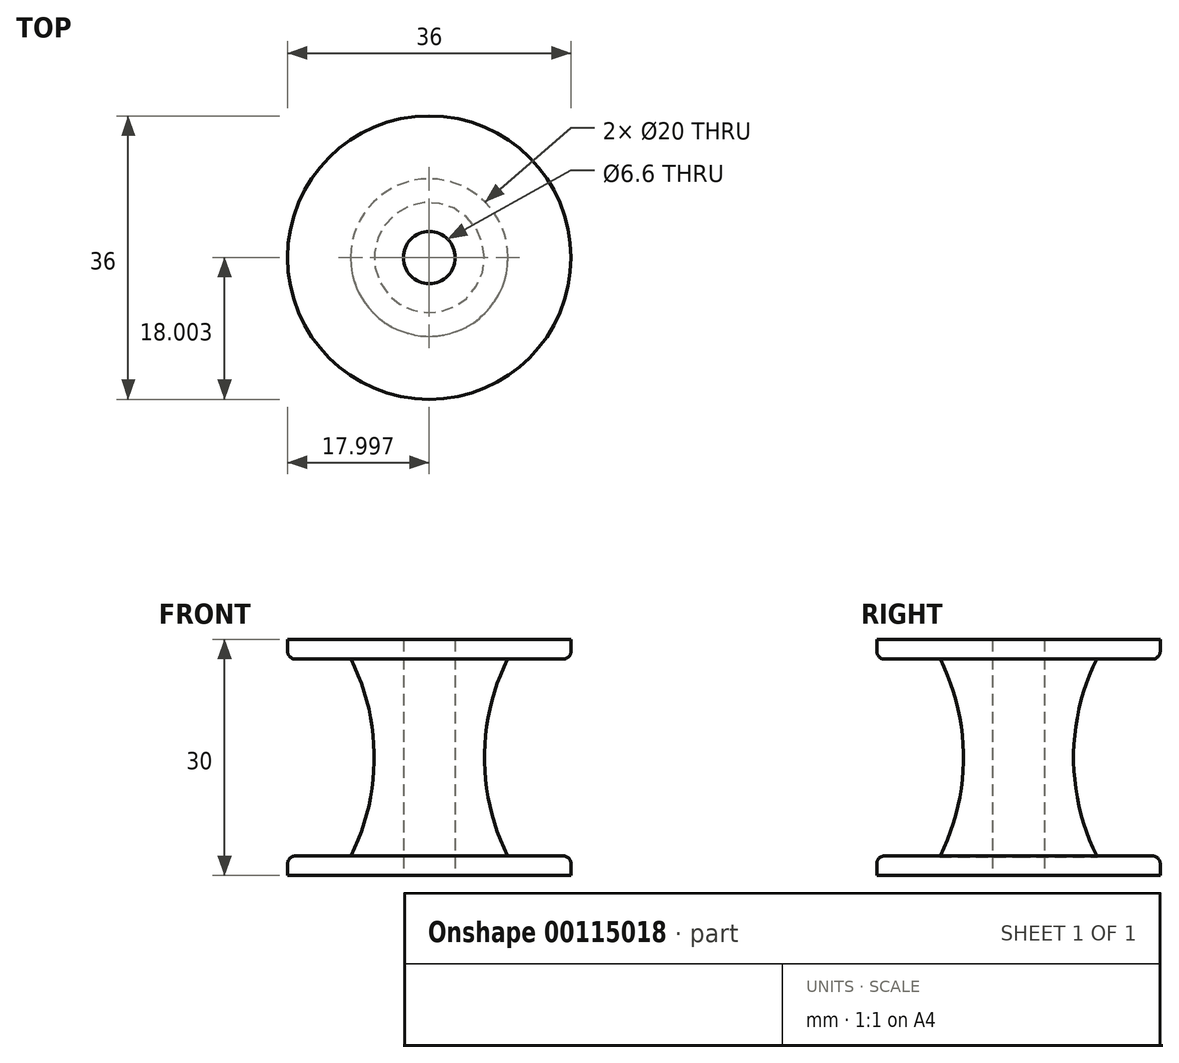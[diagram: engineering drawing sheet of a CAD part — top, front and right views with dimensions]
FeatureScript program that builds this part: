
annotation { "Feature Type Name" : "Feature", "Feature Type Description" : "" }
export const myFeature = defineFeature(function(context is Context, id is Id, definition is map)
    precondition{}
    {
        {
            var Q0;
            Q0=qCreatedBy(makeId("Top.planeOp"),FACE);
            var sketch = newSketch(context, id + "F0", { "sketchPlane" : qUnion([Q0])});
            skCircle(sketch, "E0", {"center": v(-61.26, -46.26) * mm, "radius": 3.3 * mm});
            skCircle(sketch, "E1", {"center": v(-61.26, -46.26) * mm, "radius": 10 * mm});
            skSolve(sketch);
        }
        {
            var Q0;
            Q0=makeQuery(id+"F0.imprint","IMPRINT",FACE,{"disambiguationData":[TD([[makeQuery(id+"F0.imprint","IMPRINT",EDGE,{"derivedFrom":sQuery(id+"F0.wireOp",EDGE,"E0")}),-1.0]])]});
            extrude(context, id + "F1", {"entities" : qUnion([Q0]), "depth" : 15 * mm});
        }
        {
            var Q0;
            Q0=makeQuery(id+"F0.imprint","IMPRINT",FACE,{"disambiguationData":[TD([[makeQuery(id+"F0.imprint","IMPRINT",EDGE,{"derivedFrom":sQuery(id+"F0.wireOp",EDGE,"E0")}),-1.0]])]});
            extrude(context, id + "F2", {"entities" : qUnion([Q0]), "operationType" : NewBodyOperationType.ADD, "oppositeDirection" : true, "depth" : 15 * mm});
        }
        {
            var Q0;
            Q0=sQuery(id+"F0.wireOp",VERTEX,"E0.center");
            var Q1;
            Q1=sQuery(id+"F0.wireOp",EDGE,"E1");
            cPlane(context, id + "F3", {"entities" : qUnion([Q0, Q1]), "cplaneType" : CPlaneType.CURVE_POINT, "offset" : 25 * mm, "width" : 150 * mm, "height" : 150 * mm});
        }
        {
            var Q0;
            Q0=qCreatedBy(id+"F3.planeOp",FACE);
            var sketch = newSketch(context, id + "F4", { "sketchPlane" : qUnion([Q0])});
            skCircle(sketch, "E2", {"center": v(-51.26, 0) * mm, "radius": 1.75 * mm, "construction": true});
            skLineSegment(sketch, "E3", {"start": v(-51.26, 0) * mm, "end": v(-26.26, 0) * mm, "construction": true});
            skCircle(sketch, "E4", {"center": v(-26.26, 0) * mm, "radius": 28 * mm});
            skSolve(sketch);
        }
        {
            var Q0;
            Q0=makeQuery(id+"F4.imprint","IMPRINT",FACE,{"disambiguationData":[TD([[makeQuery(id+"F4.imprint","IMPRINT",EDGE,{"derivedFrom":sQuery(id+"F4.wireOp",EDGE,"E4")}),1.0]])]});
            var Q1;
            Q1=sQuery(id+"F0.wireOp",EDGE,"E1");
            sweep(context, id + "F5", {"operationType" : NewBodyOperationType.REMOVE, "profiles" : qUnion([Q0]), "path" : qUnion([Q1])});
        }
        {
            var Q0;
            Q0=makeQuery(id+"F1.opExtrude","CAP_FACE",FACE,{"disambiguationData":[OSD([sQuery(id+"F0.wireOp",EDGE,"E0"),sQuery(id+"F0.wireOp",EDGE,"E1")])],"isStart":false});
            var sketch = newSketch(context, id + "F6", { "sketchPlane" : qUnion([Q0])});
            skCircle(sketch, "E5", {"center": v(-61.26, -46.26) * mm, "radius": 18 * mm});
            skSolve(sketch);
        }
        {
            var Q0;
            Q0=makeQuery(id+"F6.imprint","IMPRINT",FACE,{"disambiguationData":[TD([[makeQuery(id+"F6.imprint","IMPRINT",EDGE,{"derivedFrom":sQuery(id+"F6.wireOp",EDGE,"E5")}),1.0]])]});
            extrude(context, id + "F7", {"entities" : qUnion([Q0]), "operationType" : NewBodyOperationType.ADD, "oppositeDirection" : true, "depth" : 2.5 * mm});
        }
        {
            var Q0;
            Q0=makeQuery(id+"F7.opExtrude","CAP_EDGE",EDGE,{"disambiguationData":[OSD([sQuery(id+"F6.wireOp",EDGE,"E5")])],"isStart":false});
            fillet(context, id + "F8", {"entities" : qUnion([Q0]), "radius" : 1 * mm, "tangentPropagation" : true, "allowEdgeOverflow" : false});
        }
        {
            var Q0;
            Q0=makeQuery(id+"F2.opExtrude","CAP_FACE",FACE,{"disambiguationData":[OSD([sQuery(id+"F0.wireOp",EDGE,"E0"),sQuery(id+"F0.wireOp",EDGE,"E1")])],"isStart":false});
            var sketch = newSketch(context, id + "F9", { "sketchPlane" : qUnion([Q0])});
            skCircle(sketch, "E6", {"center": v(-61.26, 46.26) * mm, "radius": 18 * mm});
            skSolve(sketch);
        }
        {
            var Q0;
            Q0=makeQuery(id+"F9.imprint","IMPRINT",FACE,{"disambiguationData":[TD([[makeQuery(id+"F9.imprint","IMPRINT",EDGE,{"derivedFrom":sQuery(id+"F9.wireOp",EDGE,"E6")}),1.0]])]});
            extrude(context, id + "F10", {"entities" : qUnion([Q0]), "operationType" : NewBodyOperationType.ADD, "oppositeDirection" : true, "depth" : 2.5 * mm});
        }
        {
            var Q0;
            Q0=makeQuery(id+"F10.opExtrude","CAP_EDGE",EDGE,{"disambiguationData":[OSD([sQuery(id+"F9.wireOp",EDGE,"E6")])],"isStart":false});
            fillet(context, id + "F11", {"entities" : qUnion([Q0]), "radius" : 1 * mm, "tangentPropagation" : true, "allowEdgeOverflow" : false});
        }
    });
